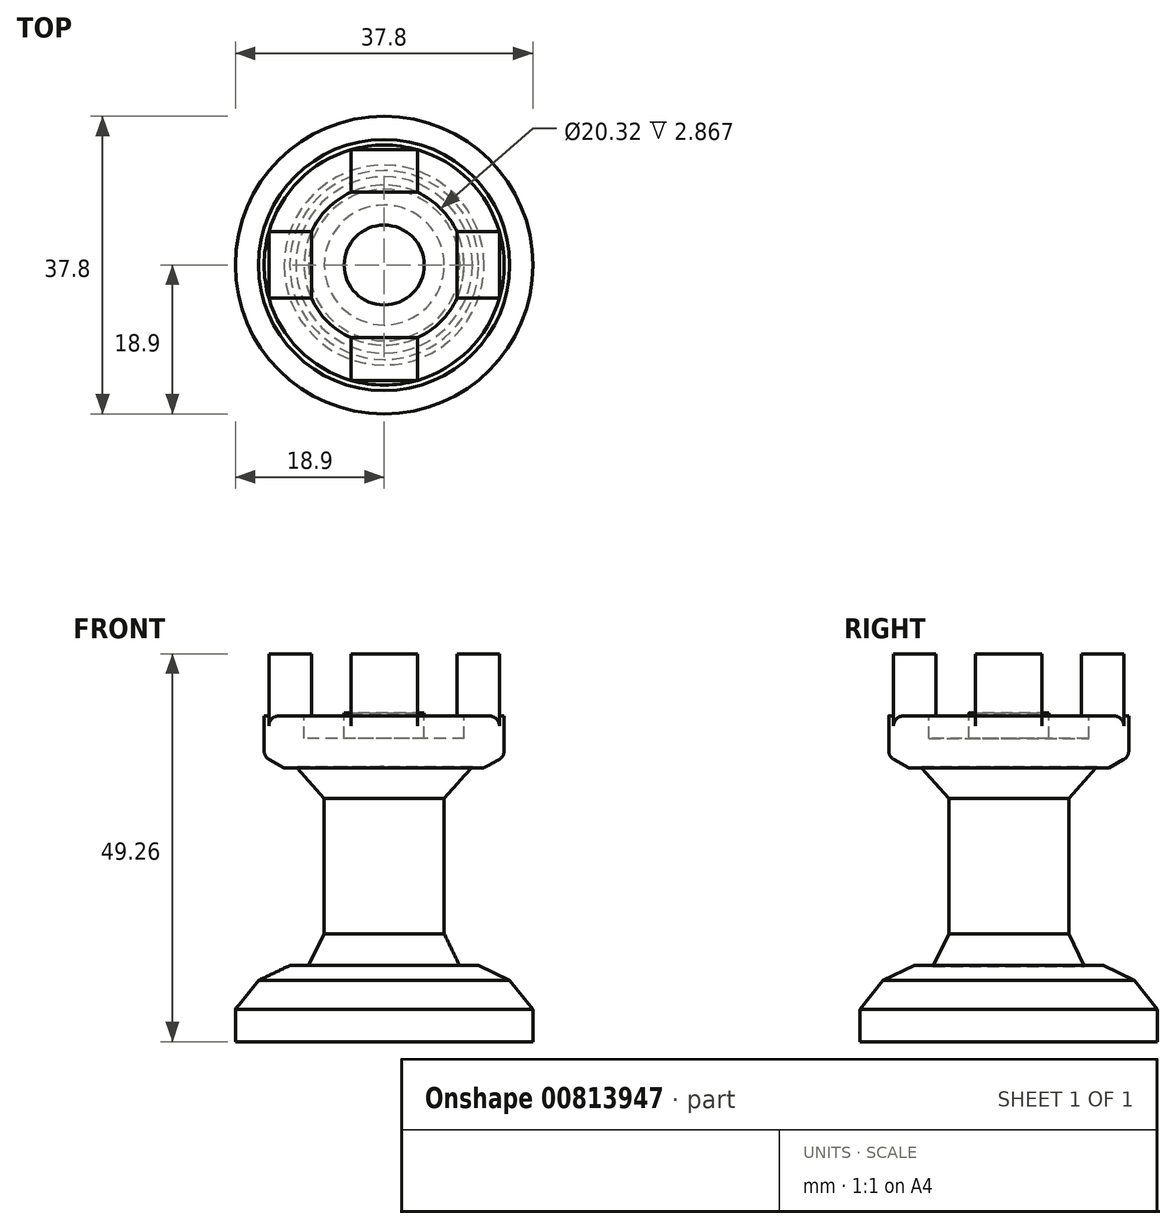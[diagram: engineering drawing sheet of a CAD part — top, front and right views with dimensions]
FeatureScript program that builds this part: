
annotation { "Feature Type Name" : "Feature", "Feature Type Description" : "" }
export const myFeature = defineFeature(function(context is Context, id is Id, definition is map)
    precondition{}
    {
        {
            var Q0;
            Q0=qCreatedBy(makeId("Front.planeOp"),FACE);
            var sketch = newSketch(context, id + "F0", { "sketchPlane" : qUnion([Q0])});
            skLineSegment(sketch, "E0", {"start": v(0, -5.91) * mm, "end": v(-18.9, -5.91) * mm});
            skLineSegment(sketch, "E1", {"start": v(-18.9, -5.91) * mm, "end": v(-18.9, -1.8) * mm});
            skLineSegment(sketch, "E2", {"start": v(-14.43, 3.76) * mm, "end": v(0, 3.76) * mm});
            skLineSegment(sketch, "E3", {"start": v(0, 3.76) * mm, "end": v(0, -5.91) * mm});
            skLineSegment(sketch, "E4", {"start": v(-14.43, 3.76) * mm, "end": v(-18.9, -1.8) * mm});
            skSolve(sketch);
        }
        {
            var Q0;
            Q0 = qSketchRegion(id + "F0", true);
            var Q1;
            Q1=sQuery(id+"F0.wireOp",EDGE,"E3");
            revolve(context, id + "F1", {"surfaceOperationType" : NewSurfaceOperationType.NEW, "entities" : qUnion([Q0]), "axis" : qUnion([Q1]), "revolveType" : RevolveType.FULL});
        }
        {
            var Q0;
            Q0=qCreatedBy(makeId("Front.planeOp"),FACE);
            var sketch = newSketch(context, id + "F2", { "sketchPlane" : qUnion([Q0])});
            skLineSegment(sketch, "E5", {"start": v(-9.62, 3.67) * mm, "end": v(-7.62, 7.8) * mm});
            skLineSegment(sketch, "E6", {"start": v(-7.62, 7.8) * mm, "end": v(-7.62, 25) * mm});
            skLineSegment(sketch, "E7", {"start": v(-7.62, 25) * mm, "end": v(-11.2, 29) * mm});
            skLineSegment(sketch, "E8", {"start": v(-11.2, 29) * mm, "end": v(0, 29) * mm});
            skLineSegment(sketch, "E9", {"start": v(0, 29) * mm, "end": v(0, 25.06) * mm});
            skLineSegment(sketch, "E10", {"start": v(0, 25.06) * mm, "end": v(-7.62, 25.06) * mm});
            skLineSegment(sketch, "E11", {"start": v(0, 25.06) * mm, "end": v(0, 0) * mm});
            skLineSegment(sketch, "E12", {"start": v(-9.62, 3.67) * mm, "end": v(0, 3.67) * mm});
            skLineSegment(sketch, "E13", {"start": v(0, 3.67) * mm, "end": v(0, 7.8) * mm});
            skLineSegment(sketch, "E14", {"start": v(0, 7.8) * mm, "end": v(-7.62, 7.8) * mm});
            skSolve(sketch);
        }
        {
            var Q0;
            Q0 = qSketchRegion(id + "F2", true);
            var Q1;
            Q1=sQuery(id+"F2.wireOp",EDGE,"E11");
            revolve(context, id + "F3", {"surfaceOperationType" : NewSurfaceOperationType.NEW, "entities" : qUnion([Q0]), "axis" : qUnion([Q1]), "revolveType" : RevolveType.FULL});
        }
        {
            var Q0;
            Q0=qCreatedBy(makeId("Front.planeOp"),FACE);
            var sketch = newSketch(context, id + "F4", { "sketchPlane" : qUnion([Q0])});
            skLineSegment(sketch, "E15", {"start": v(-12.7, 28.87) * mm, "end": v(-15.24, 30.28) * mm});
            skLineSegment(sketch, "E16", {"start": v(-15.24, 30.28) * mm, "end": v(-15.24, 35.48) * mm});
            skLineSegment(sketch, "E17", {"start": v(-15.24, 35.48) * mm, "end": v(-10.16, 35.48) * mm});
            skLineSegment(sketch, "E18", {"start": v(-10.16, 35.48) * mm, "end": v(-10.16, 32.61) * mm});
            skLineSegment(sketch, "E19", {"start": v(-10.16, 32.61) * mm, "end": v(-5.08, 32.61) * mm});
            skLineSegment(sketch, "E20", {"start": v(-5.08, 32.61) * mm, "end": v(-5.08, 35.84) * mm});
            skLineSegment(sketch, "E21", {"start": v(-5.08, 35.84) * mm, "end": v(0, 35.84) * mm});
            skLineSegment(sketch, "E22", {"start": v(0, 35.84) * mm, "end": v(0, 29.03) * mm});
            skLineSegment(sketch, "E23", {"start": v(0, 29.03) * mm, "end": v(-12.7, 28.87) * mm});
            skSolve(sketch);
        }
        {
            var Q0;
            Q0 = qSketchRegion(id + "F4", true);
            var Q1;
            Q1=sQuery(id+"F4.wireOp",EDGE,"E22");
            revolve(context, id + "F5", {"surfaceOperationType" : NewSurfaceOperationType.NEW, "entities" : qUnion([Q0]), "axis" : qUnion([Q1]), "revolveType" : RevolveType.FULL});
        }
        {
            var Q0;
            Q0=makeQuery(id+"F5.opRevolve","SWEPT_FACE",FACE,{"disambiguationData":[OSD([sQuery(id+"F4.wireOp",EDGE,"E17")])]});
            var sketch = newSketch(context, id + "F6", { "sketchPlane" : qUnion([Q0])});
            skLineSegment(sketch, "E24", {"start": v(-4.22, 14.64) * mm, "end": v(-4.22, 9.24) * mm});
            skLineSegment(sketch, "E25", {"start": v(-4.22, 9.24) * mm, "end": v(4.22, 9.24) * mm});
            skLineSegment(sketch, "E26", {"start": v(4.22, 9.24) * mm, "end": v(4.22, 14.64) * mm});
            skLineSegment(sketch, "E27", {"start": v(4.22, 14.64) * mm, "end": v(-4.22, 14.64) * mm});
            skLineSegment(sketch, "E28", {"start": v(9.24, 4.22) * mm, "end": v(9.24, -4.22) * mm});
            skLineSegment(sketch, "E29", {"start": v(9.24, -4.22) * mm, "end": v(14.64, -4.22) * mm});
            skLineSegment(sketch, "E30", {"start": v(14.64, -4.22) * mm, "end": v(14.64, 4.22) * mm});
            skLineSegment(sketch, "E31", {"start": v(14.64, 4.22) * mm, "end": v(9.24, 4.22) * mm});
            skLineSegment(sketch, "E32", {"start": v(-9.24, 4.22) * mm, "end": v(-9.24, -4.22) * mm});
            skLineSegment(sketch, "E33", {"start": v(-9.24, -4.22) * mm, "end": v(-14.64, -4.22) * mm});
            skLineSegment(sketch, "E34", {"start": v(-14.64, -4.22) * mm, "end": v(-14.64, 4.22) * mm});
            skLineSegment(sketch, "E35", {"start": v(-14.64, 4.22) * mm, "end": v(-9.24, 4.22) * mm});
            skLineSegment(sketch, "E36", {"start": v(-4.22, -9.24) * mm, "end": v(4.22, -9.24) * mm});
            skLineSegment(sketch, "E37", {"start": v(4.22, -9.24) * mm, "end": v(4.22, -14.64) * mm});
            skLineSegment(sketch, "E38", {"start": v(4.22, -14.64) * mm, "end": v(-4.22, -14.64) * mm});
            skLineSegment(sketch, "E39", {"start": v(-4.22, -14.64) * mm, "end": v(-4.22, -9.24) * mm});
            skSolve(sketch);
        }
        {
            var Q0;
            Q0 = qSketchRegion(id + "F6", true);
            extrude(context, id + "F7", {"entities" : qUnion([Q0]), "operationType" : NewBodyOperationType.ADD, "depth" : 7.87 * mm, "offsetDistance" : 25.4 * mm});
        }
        {
            var Q0;
            Q0=makeQuery(id+"F5.opRevolve","SWEPT_FACE",FACE,{"disambiguationData":[OSD([sQuery(id+"F4.wireOp",EDGE,"E16")])]});
            fillet(context, id + "F8", {"entities" : qUnion([Q0]), "radius" : 1.27 * mm, "tangentPropagation" : true, "allowEdgeOverflow" : false});
        }
        {
            var Q0;
            Q0=makeQuery(id+"F1.opRevolve","SWEPT_EDGE",EDGE,{"disambiguationData":[OSD([sQuery(id+"F0.wireOp",EDGE,"E2"),sQuery(id+"F0.wireOp",EDGE,"E4")])]});
            chamfer(context, id + "F9", {"entities" : qUnion([Q0]), "width" : 5.08 * mm, "tangentPropagation" : true});
        }
    });
